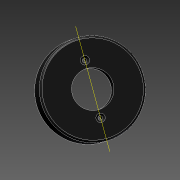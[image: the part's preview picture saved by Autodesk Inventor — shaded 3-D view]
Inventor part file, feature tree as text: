
AUTODESK INVENTOR PART (.ipt)
format: ipt  version: 2013 (Build 170138000, 138)  size: 108,032 bytes
history: native  units: mm
features: sketch x3, extrude x2, other x1, hole x1, fillet x1
ambient origin geometry x8: Origin, YZ Plane, XZ Plane, XY Plane, X Axis, Y Axis, Z Axis, Center Point
bodies: Volumenkörper1 (feature_tree)
feature tree (8):
  extrude  "Extrusion1"  Depth=9.0mm
  other  "Arbeitsachse1"
  extrude  "Extrusion2"  Depth=32.0mm
  hole  "Bohrung1"  [1 undecoded]
  fillet  "Rundung1"  Radius=12.5mm
  sketch  "Skizze1"  dims[d0=45.0mm d2=9.0mm]
  sketch  "Skizze3"  dims[d3=15.0mm d4=0.0mm d5=32.0mm]
  sketch  "Skizze4"  dims[d6=8.0mm d7=0.0mm d8=12.5mm d9=12.5mm d10=2.0mm d11=6.0mm d12=4.0mm d13=2.0mm d14=90.0deg d15=8.0mm d16=20.594885mm d17=1.0mm]
note: 1 required parameter value undecoded (feature->parameter linkage not recoverable at this tier; creation-order binding heuristic only, values carry confidence <= 0.55)
